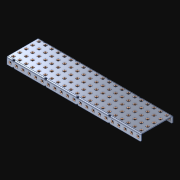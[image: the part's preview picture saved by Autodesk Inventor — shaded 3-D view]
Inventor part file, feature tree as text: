
AUTODESK INVENTOR PART (.ipt)
format: ipt  version: 2021 (Build 250183000, 183)  size: 2,027,008 bytes
history: native  units: in
note: dims shown in document units (in); Inventor stores cm internally (conversion verified against a paired STEP export)
features: extrude x148, other x148, sketch x4, pattern_linear x3
ambient origin geometry x8: Origin, YZ Plane, XZ Plane, XY Plane, X Axis, Y Axis, Z Axis, Center Point
bodies: Solid1 (feature_tree)
feature tree (303):
  pattern_linear  "Rectangular Pattern1"  Spacing1=0.182in  [1 undecoded]
  pattern_linear  "Rectangular Pattern2"  Spacing1=0.046in  [1 undecoded]
  pattern_linear  "Rectangular Pattern3"  Spacing1=0.5in  [1 undecoded]
  extrude  "Extrusion1"  Depth=0.046in
  sketch  "Sketch1"  dims[d0=0.182in]
  other  "Srf1"
  sketch  "Sketch2"  dims[d1=0.046in d2=0.0in]
  other  "Srf2"
  sketch  "Sketch3"  dims[d3=0.182in]
  other  "Srf3"
  other  "Srf4"
  other  "Srf5"
  other  "Srf6"
  other  "Srf7"
  other  "Srf8"
  other  "Srf9"
  other  "Srf10"
  other  "Srf11"
  other  "Srf12"
  other  "Srf13"
  other  "Srf14"
  other  "Srf15"
  other  "Srf16"
  other  "Srf17"
  other  "Srf18"
  other  "Srf19"
  other  "Srf20"
  other  "Srf21"
  other  "Srf22"
  other  "Srf23"
  other  "Srf38"
  other  "Srf39"
  other  "Srf40"
  other  "Srf41"
  other  "Srf42"
  other  "Srf43"
  other  "Srf44"
  other  "Srf45"
  other  "Srf46"
  other  "Srf47"
  other  "Srf48"
  other  "Srf49"
  other  "Srf50"
  other  "Srf51"
  other  "Srf52"
  other  "Srf53"
  other  "Srf54"
  other  "Srf55"
  other  "Srf56"
  other  "Srf57"
  other  "Srf72"
  other  "Srf73"
  other  "Srf74"
  other  "Srf75"
  other  "Srf76"
  other  "Srf77"
  other  "Srf78"
  other  "Srf79"
  other  "Srf80"
  other  "Srf81"
  other  "Srf82"
  other  "Srf83"
  other  "Srf84"
  other  "Srf85"
  other  "Srf86"
  other  "Srf87"
  other  "Srf88"
  other  "Srf89"
  other  "Srf90"
  other  "Srf91"
  other  "Srf92"
  other  "Srf107"
  other  "Srf108"
  other  "Srf109"
  other  "Srf110"
  other  "Srf111"
  other  "Srf112"
  other  "Srf113"
  other  "Srf114"
  other  "Srf115"
  other  "Srf116"
  other  "Srf117"
  other  "Srf118"
  other  "Srf119"
  other  "Srf120"
  other  "Srf121"
  other  "Srf122"
  other  "Srf123"
  other  "Srf124"
  other  "Srf125"
  other  "Srf126"
  other  "Srf127"
  other  "Srf142"
  other  "Srf143"
  other  "Srf144"
  other  "Srf145"
  other  "Srf146"
  other  "Srf147"
  other  "Srf148"
  other  "Srf149"
  other  "Srf150"
  other  "Srf151"
  other  "Srf152"
  other  "Srf153"
  other  "Srf154"
  other  "Srf155"
  other  "Srf156"
  other  "Srf157"
  other  "Srf158"
  other  "Srf159"
  other  "Srf160"
  other  "Srf161"
  other  "Srf162"
  other  "Srf177"
  other  "Srf178"
  other  "Srf179"
  other  "Srf180"
  other  "Srf181"
  other  "Srf182"
  other  "Srf183"
  other  "Srf184"
  other  "Srf185"
  other  "Srf186"
  other  "Srf187"
  other  "Srf188"
  other  "Srf189"
  other  "Srf190"
  other  "Srf191"
  other  "Srf192"
  other  "Srf193"
  other  "Srf194"
  other  "Srf195"
  other  "Srf196"
  other  "Srf197"
  other  "Srf212"
  other  "Srf213"
  other  "Srf214"
  other  "Srf215"
  other  "Srf216"
  other  "Srf217"
  other  "Srf218"
  other  "Srf219"
  other  "Srf220"
  other  "Srf221"
  other  "Srf222"
  other  "Srf223"
  other  "Srf224"
  other  "Srf225"
  other  "Srf226"
  other  "Srf227"
  other  "Srf228"
  other  "Srf229"
  other  "Srf230"
  other  "Srf231"
  sketch  "Sketch4"  dims[d4=0.046in d5=0.0in d6=0.182in d7=0.046in d8=0.0in d11=0.5in d12=8.2677in d14=0.5in d15=1.9685in d17=0.5in d18=8.2677in d20=0.5in d21=7.0in d22=0.0in]
  parser-record x1  (decoder bookkeeping rows leaked as tree rows — omitted from the tree; the rows remain in map.json)
  extrude  "ExtrusionSrf1"  Depth=0.046in
  extrude  "ExtrusionSrf2"  Depth=0.046in
  extrude  "ExtrusionSrf3"  Depth=0.046in
  extrude  "ExtrusionSrf4"  Depth=0.046in
  extrude  "ExtrusionSrf5"  Depth=0.046in
  extrude  "ExtrusionSrf6"  TaperAngle=0.0deg  [1 undecoded]
  extrude  "ExtrusionSrf7"  [1 undecoded]
  extrude  "ExtrusionSrf8"  [1 undecoded]
  extrude  "ExtrusionSrf9"  [1 undecoded]
  extrude  "ExtrusionSrf10"  [1 undecoded]
  extrude  "ExtrusionSrf11"  [1 undecoded]
  extrude  "ExtrusionSrf12"  [1 undecoded]
  extrude  "ExtrusionSrf13"  [1 undecoded]
  extrude  "ExtrusionSrf14"  [1 undecoded]
  extrude  "ExtrusionSrf15"  [1 undecoded]
  extrude  "ExtrusionSrf16"  [1 undecoded]
  extrude  "ExtrusionSrf17"  [1 undecoded]
  extrude  "ExtrusionSrf18"  [1 undecoded]
  extrude  "ExtrusionSrf19"  [1 undecoded]
  extrude  "ExtrusionSrf20"  [1 undecoded]
  extrude  "ExtrusionSrf21"  [1 undecoded]
  extrude  "ExtrusionSrf22"  [1 undecoded]
  extrude  "ExtrusionSrf23"  [1 undecoded]
  extrude  "ExtrusionSrf38"  [1 undecoded]
  extrude  "ExtrusionSrf39"  [1 undecoded]
  extrude  "ExtrusionSrf40"  [1 undecoded]
  extrude  "ExtrusionSrf41"  [1 undecoded]
  extrude  "ExtrusionSrf42"  [1 undecoded]
  extrude  "ExtrusionSrf43"  [1 undecoded]
  extrude  "ExtrusionSrf44"  [1 undecoded]
  extrude  "ExtrusionSrf45"  [1 undecoded]
  extrude  "ExtrusionSrf46"  [1 undecoded]
  extrude  "ExtrusionSrf47"  [1 undecoded]
  extrude  "ExtrusionSrf48"  [1 undecoded]
  extrude  "ExtrusionSrf49"  [1 undecoded]
  extrude  "ExtrusionSrf50"  [1 undecoded]
  extrude  "ExtrusionSrf51"  [1 undecoded]
  extrude  "ExtrusionSrf52"  [1 undecoded]
  extrude  "ExtrusionSrf53"  [1 undecoded]
  extrude  "ExtrusionSrf54"  [1 undecoded]
  extrude  "ExtrusionSrf55"  [1 undecoded]
  extrude  "ExtrusionSrf56"  [1 undecoded]
  extrude  "ExtrusionSrf57"  [1 undecoded]
  extrude  "ExtrusionSrf72"  [1 undecoded]
  extrude  "ExtrusionSrf73"  [1 undecoded]
  extrude  "ExtrusionSrf74"  [1 undecoded]
  extrude  "ExtrusionSrf75"  [1 undecoded]
  extrude  "ExtrusionSrf76"  [1 undecoded]
  extrude  "ExtrusionSrf77"  [1 undecoded]
  extrude  "ExtrusionSrf78"  [1 undecoded]
  extrude  "ExtrusionSrf79"  [1 undecoded]
  extrude  "ExtrusionSrf80"  [1 undecoded]
  extrude  "ExtrusionSrf81"  [1 undecoded]
  extrude  "ExtrusionSrf82"  [1 undecoded]
  extrude  "ExtrusionSrf83"  [1 undecoded]
  extrude  "ExtrusionSrf84"  [1 undecoded]
  extrude  "ExtrusionSrf85"  [1 undecoded]
  extrude  "ExtrusionSrf86"  [1 undecoded]
  extrude  "ExtrusionSrf87"  [1 undecoded]
  extrude  "ExtrusionSrf88"  [1 undecoded]
  extrude  "ExtrusionSrf89"  [1 undecoded]
  extrude  "ExtrusionSrf90"  [1 undecoded]
  extrude  "ExtrusionSrf91"  [1 undecoded]
  extrude  "ExtrusionSrf92"  [1 undecoded]
  extrude  "ExtrusionSrf107"  [1 undecoded]
  extrude  "ExtrusionSrf108"  [1 undecoded]
  extrude  "ExtrusionSrf109"  [1 undecoded]
  extrude  "ExtrusionSrf110"  [1 undecoded]
  extrude  "ExtrusionSrf111"  [1 undecoded]
  extrude  "ExtrusionSrf112"  [1 undecoded]
  extrude  "ExtrusionSrf113"  [1 undecoded]
  extrude  "ExtrusionSrf114"  [1 undecoded]
  extrude  "ExtrusionSrf115"  [1 undecoded]
  extrude  "ExtrusionSrf116"  [1 undecoded]
  extrude  "ExtrusionSrf117"  [1 undecoded]
  extrude  "ExtrusionSrf118"  [1 undecoded]
  extrude  "ExtrusionSrf119"  [1 undecoded]
  extrude  "ExtrusionSrf120"  [1 undecoded]
  extrude  "ExtrusionSrf121"  [1 undecoded]
  extrude  "ExtrusionSrf122"  [1 undecoded]
  extrude  "ExtrusionSrf123"  [1 undecoded]
  extrude  "ExtrusionSrf124"  [1 undecoded]
  extrude  "ExtrusionSrf125"  [1 undecoded]
  extrude  "ExtrusionSrf126"  [1 undecoded]
  extrude  "ExtrusionSrf127"  [1 undecoded]
  extrude  "ExtrusionSrf142"  [1 undecoded]
  extrude  "ExtrusionSrf143"  [1 undecoded]
  extrude  "ExtrusionSrf144"  [1 undecoded]
  extrude  "ExtrusionSrf145"  [1 undecoded]
  extrude  "ExtrusionSrf146"  [1 undecoded]
  extrude  "ExtrusionSrf147"  [1 undecoded]
  extrude  "ExtrusionSrf148"  [1 undecoded]
  extrude  "ExtrusionSrf149"  [1 undecoded]
  extrude  "ExtrusionSrf150"  [1 undecoded]
  extrude  "ExtrusionSrf151"  [1 undecoded]
  extrude  "ExtrusionSrf152"  [1 undecoded]
  extrude  "ExtrusionSrf153"  [1 undecoded]
  extrude  "ExtrusionSrf154"  [1 undecoded]
  extrude  "ExtrusionSrf155"  [1 undecoded]
  extrude  "ExtrusionSrf156"  [1 undecoded]
  extrude  "ExtrusionSrf157"  [1 undecoded]
  extrude  "ExtrusionSrf158"  [1 undecoded]
  extrude  "ExtrusionSrf159"  [1 undecoded]
  extrude  "ExtrusionSrf160"  [1 undecoded]
  extrude  "ExtrusionSrf161"  [1 undecoded]
  extrude  "ExtrusionSrf162"  [1 undecoded]
  extrude  "ExtrusionSrf177"  [1 undecoded]
  extrude  "ExtrusionSrf178"  [1 undecoded]
  extrude  "ExtrusionSrf179"  [1 undecoded]
  extrude  "ExtrusionSrf180"  [1 undecoded]
  extrude  "ExtrusionSrf181"  [1 undecoded]
  extrude  "ExtrusionSrf182"  [1 undecoded]
  extrude  "ExtrusionSrf183"  [1 undecoded]
  extrude  "ExtrusionSrf184"  [1 undecoded]
  extrude  "ExtrusionSrf185"  [1 undecoded]
  extrude  "ExtrusionSrf186"  [1 undecoded]
  extrude  "ExtrusionSrf187"  [1 undecoded]
  extrude  "ExtrusionSrf188"  [1 undecoded]
  extrude  "ExtrusionSrf189"  [1 undecoded]
  extrude  "ExtrusionSrf190"  [1 undecoded]
  extrude  "ExtrusionSrf191"  [1 undecoded]
  extrude  "ExtrusionSrf192"  [1 undecoded]
  extrude  "ExtrusionSrf193"  [1 undecoded]
  extrude  "ExtrusionSrf194"  [1 undecoded]
  extrude  "ExtrusionSrf195"  [1 undecoded]
  extrude  "ExtrusionSrf196"  [1 undecoded]
  extrude  "ExtrusionSrf197"  [1 undecoded]
  extrude  "ExtrusionSrf212"  [1 undecoded]
  extrude  "ExtrusionSrf213"  [1 undecoded]
  extrude  "ExtrusionSrf214"  [1 undecoded]
  extrude  "ExtrusionSrf215"  [1 undecoded]
  extrude  "ExtrusionSrf216"  [1 undecoded]
  extrude  "ExtrusionSrf217"  [1 undecoded]
  extrude  "ExtrusionSrf218"  [1 undecoded]
  extrude  "ExtrusionSrf219"  [1 undecoded]
  extrude  "ExtrusionSrf220"  [1 undecoded]
  extrude  "ExtrusionSrf221"  [1 undecoded]
  extrude  "ExtrusionSrf222"  [1 undecoded]
  extrude  "ExtrusionSrf223"  [1 undecoded]
  extrude  "ExtrusionSrf224"  [1 undecoded]
  extrude  "ExtrusionSrf225"  [1 undecoded]
  extrude  "ExtrusionSrf226"  [1 undecoded]
  extrude  "ExtrusionSrf227"  [1 undecoded]
  extrude  "ExtrusionSrf228"  [1 undecoded]
  extrude  "ExtrusionSrf229"  [1 undecoded]
  extrude  "ExtrusionSrf230"  [1 undecoded]
  extrude  "ExtrusionSrf231"  [1 undecoded]
note: 145 required parameter values undecoded (feature->parameter linkage not recoverable at this tier; creation-order binding heuristic only, values carry confidence <= 0.55)
